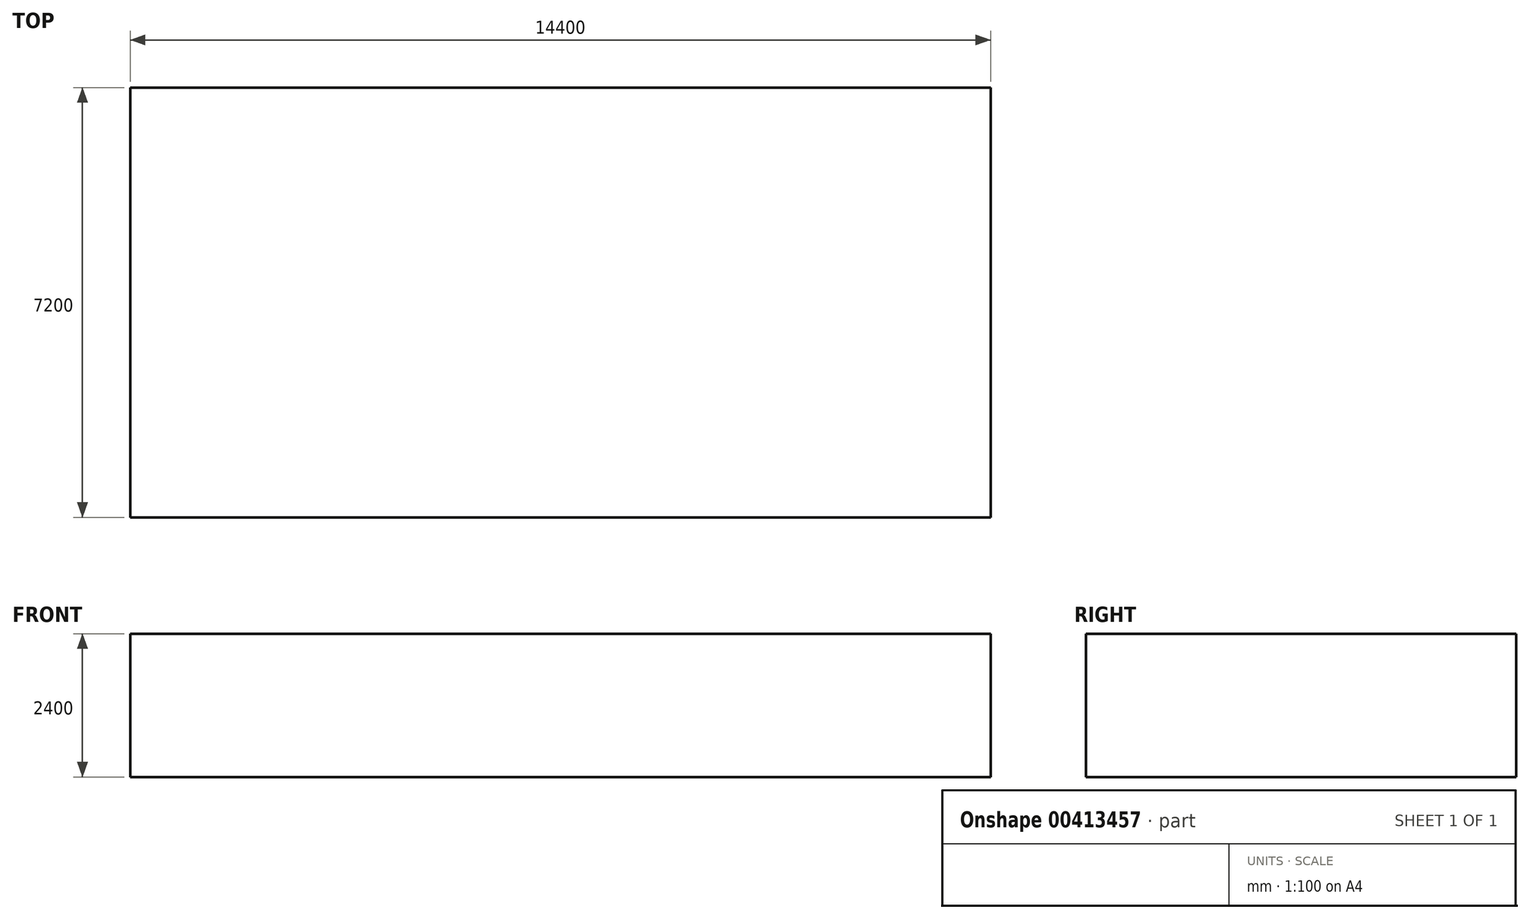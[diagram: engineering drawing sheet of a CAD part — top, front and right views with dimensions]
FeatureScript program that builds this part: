
annotation { "Feature Type Name" : "Feature", "Feature Type Description" : "" }
export const myFeature = defineFeature(function(context is Context, id is Id, definition is map)
    precondition{}
    {
        {
            var Q0;
            Q0=qCreatedBy(makeId("Top.planeOp"),FACE);
            var sketch = newSketch(context, id + "F0", { "sketchPlane" : qUnion([Q0])});
            skLineSegment(sketch, "E0.bottom", {"start": v(7200, 3600) * mm, "end": v(-7200, 3600) * mm});
            skLineSegment(sketch, "E0.top", {"start": v(7200, -3600) * mm, "end": v(-7200, -3600) * mm});
            skLineSegment(sketch, "E0.left", {"start": v(7200, 3600) * mm, "end": v(7200, -3600) * mm});
            skLineSegment(sketch, "E0.right", {"start": v(-7200, 3600) * mm, "end": v(-7200, -3600) * mm});
            skPoint(sketch, "E0.middle", {"position": v(0, 0) * mm});
            skSolve(sketch);
        }
        {
            var Q0;
            Q0 = qSketchRegion(id + "F0", true);
            var Q1;
            Q1=makeQuery(id+"F0.imprint","IMPRINT",FACE,{"disambiguationData":[TD([[makeQuery(id+"F0.imprint","IMPRINT",EDGE,{"derivedFrom":sQuery(id+"F0.wireOp",EDGE,"E0.bottom")}),1.0]])]});
            extrude(context, id + "F1", {"entities" : qUnion([Q0, Q1]), "depth" : 2400 * mm});
        }
    });
